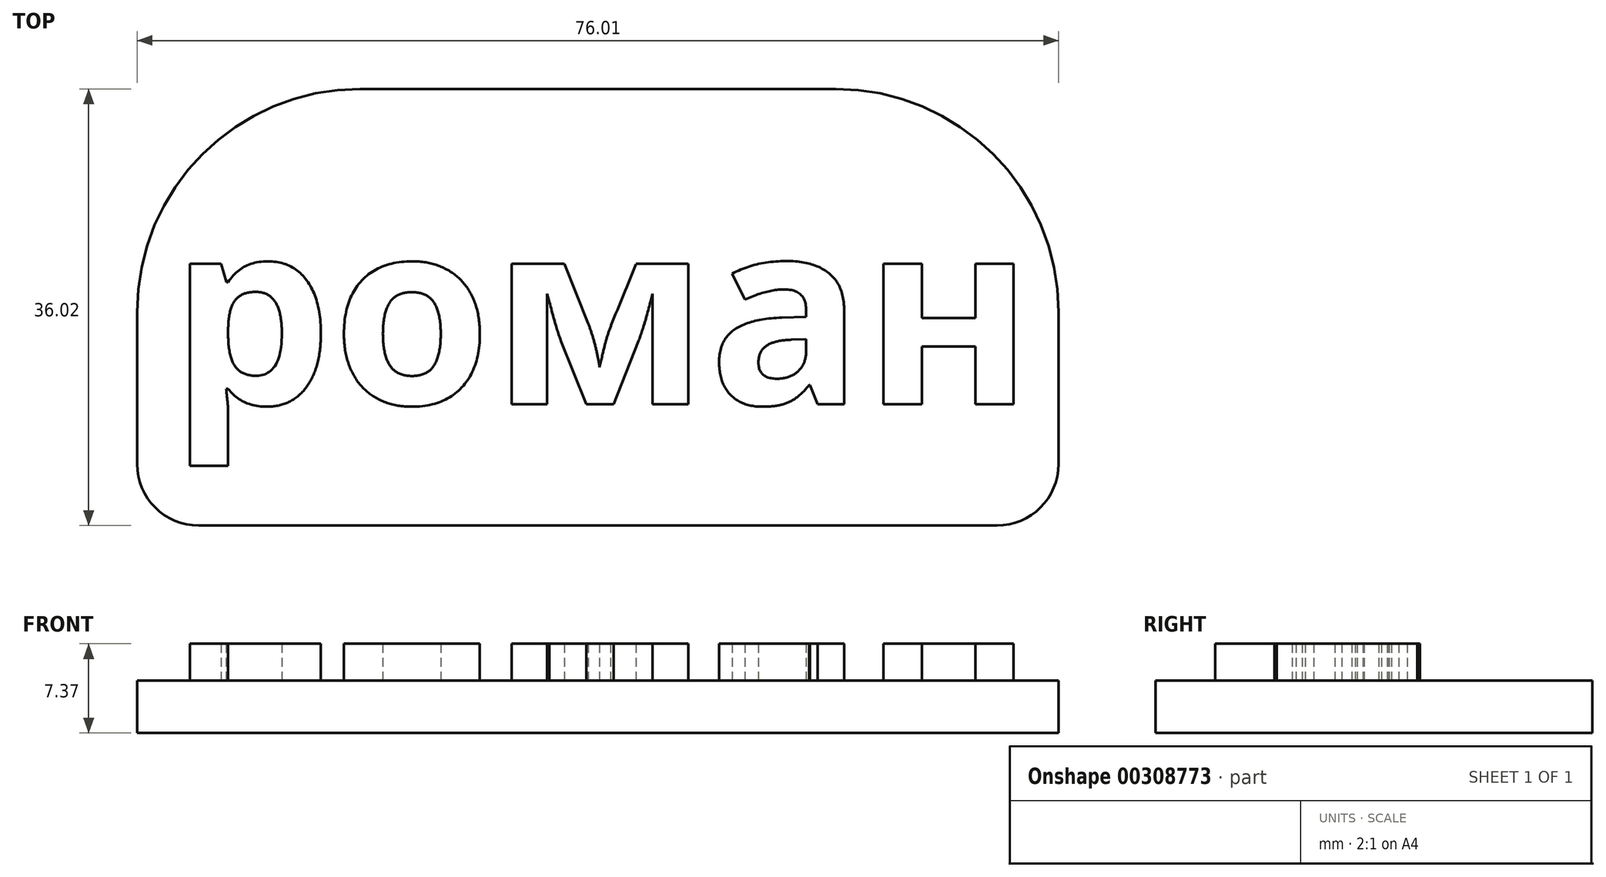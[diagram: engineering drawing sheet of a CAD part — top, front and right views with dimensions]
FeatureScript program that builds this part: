
annotation { "Feature Type Name" : "Feature", "Feature Type Description" : "" }
export const myFeature = defineFeature(function(context is Context, id is Id, definition is map)
    precondition{}
    {
        {
            var Q0;
            Q0=qCreatedBy(makeId("Top.planeOp"),FACE);
            var sketch = newSketch(context, id + "F0", { "sketchPlane" : qUnion([Q0])});
            skLineSegment(sketch, "E0.bottom", {"start": v(-32.74, 17.46) * mm, "end": v(43.46, 17.46) * mm});
            skLineSegment(sketch, "E0.top", {"start": v(-32.74, -18.4) * mm, "end": v(43.46, -18.4) * mm});
            skLineSegment(sketch, "E0.left", {"start": v(-32.74, 17.46) * mm, "end": v(-32.74, -18.4) * mm});
            skLineSegment(sketch, "E0.right", {"start": v(43.46, 17.46) * mm, "end": v(43.46, -18.4) * mm});
            skText(sketch, "E1", { "text": "роман", "fontName": "OpenSans-Bold.ttf"});
            const initialGuessF0  = {"E1": [-0.03, -0.00842, 1, 0, 0.01526]};
            skSetInitialGuess(sketch, initialGuessF0);
            skSolve(sketch);
        }
        {
            var Q0;
            Q0=makeQuery(id+"F0.imprint","IMPRINT",FACE,{"disambiguationData":[TD([[makeQuery(id+"F0.imprint","IMPRINT",EDGE,{"derivedFrom":sQuery(id+"F0.wireOp",EDGE,"E0.bottom")}),-1.0]])]});
            var sketch = newSketch(context, id + "F1", { "sketchPlane" : qUnion([Q0])});
            skLineSegment(sketch, "E2.bottom", {"start": v(-32.7, 17.6) * mm, "end": v(43.32, 17.6) * mm});
            skLineSegment(sketch, "E2.top", {"start": v(-32.7, -18.43) * mm, "end": v(43.32, -18.43) * mm});
            skLineSegment(sketch, "E2.left", {"start": v(-32.7, 17.6) * mm, "end": v(-32.7, -18.43) * mm});
            skLineSegment(sketch, "E2.right", {"start": v(43.32, 17.6) * mm, "end": v(43.32, -18.43) * mm});
            skSolve(sketch);
        }
        {
            var Q0;
            Q0 = qSketchRegion(id + "F1", true);
            extrude(context, id + "F2", {"entities" : qUnion([Q0]), "depth" : 4.32 * mm});
        }
        {
            var Q0;
            Q0=makeQuery(id+"F0.imprint","IMPRINT",FACE,{"disambiguationData":[TD([[makeQuery(id+"F0.imprint","IMPRINT",EDGE,{"derivedFrom":sQuery(id+"F0.wireOp",EDGE,"E1.sketch_text.stroke-0")}),-1.0]])]});
            var Q1;
            Q1=makeQuery(id+"F0.imprint","IMPRINT",FACE,{"disambiguationData":[TD([[makeQuery(id+"F0.imprint","IMPRINT",EDGE,{"derivedFrom":sQuery(id+"F0.wireOp",EDGE,"E1.sketch_text.stroke-23")}),-1.0]])]});
            var Q2;
            Q2=makeQuery(id+"F0.imprint","IMPRINT",FACE,{"disambiguationData":[TD([[makeQuery(id+"F0.imprint","IMPRINT",EDGE,{"derivedFrom":sQuery(id+"F0.wireOp",EDGE,"E1.sketch_text.stroke-41")}),-1.0]])]});
            var Q3;
            Q3=makeQuery(id+"F0.imprint","IMPRINT",FACE,{"disambiguationData":[TD([[makeQuery(id+"F0.imprint","IMPRINT",EDGE,{"derivedFrom":sQuery(id+"F0.wireOp",EDGE,"E1.sketch_text.stroke-62")}),-1.0]])]});
            var Q4;
            Q4=makeQuery(id+"F0.imprint","IMPRINT",FACE,{"disambiguationData":[TD([[makeQuery(id+"F0.imprint","IMPRINT",EDGE,{"derivedFrom":sQuery(id+"F0.wireOp",EDGE,"E1.sketch_text.stroke-87")}),-1.0]])]});
            extrude(context, id + "F3", {"entities" : qUnion([Q0, Q1, Q2, Q3, Q4]), "operationType" : NewBodyOperationType.ADD, "depth" : 7.37 * mm});
        }
        {
            var Q0;
            Q0=makeQuery(id+"F2.opExtrude","SWEPT_EDGE",EDGE,{"disambiguationData":[OSD([sQuery(id+"F1.wireOp",EDGE,"E2.bottom"),sQuery(id+"F1.wireOp",EDGE,"E2.left")])]});
            var Q1;
            Q1=makeQuery(id+"F2.opExtrude","SWEPT_EDGE",EDGE,{"disambiguationData":[OSD([sQuery(id+"F1.wireOp",EDGE,"E2.bottom"),sQuery(id+"F1.wireOp",EDGE,"E2.right")])]});
            fillet(context, id + "F4", {"entities" : qUnion([Q0, Q1]), "radius" : 18.4 * mm, "tangentPropagation" : true, "allowEdgeOverflow" : false});
        }
        {
            var Q0;
            Q0=makeQuery(id+"F2.opExtrude","SWEPT_EDGE",EDGE,{"disambiguationData":[OSD([sQuery(id+"F1.wireOp",EDGE,"E2.top"),sQuery(id+"F1.wireOp",EDGE,"E2.left")])]});
            var Q1;
            Q1=makeQuery(id+"F2.opExtrude","SWEPT_EDGE",EDGE,{"disambiguationData":[OSD([sQuery(id+"F1.wireOp",EDGE,"E2.top"),sQuery(id+"F1.wireOp",EDGE,"E2.right")])]});
            fillet(context, id + "F5", {"entities" : qUnion([Q0, Q1]), "radius" : 5.08 * mm, "tangentPropagation" : true, "allowEdgeOverflow" : false});
        }
    });
